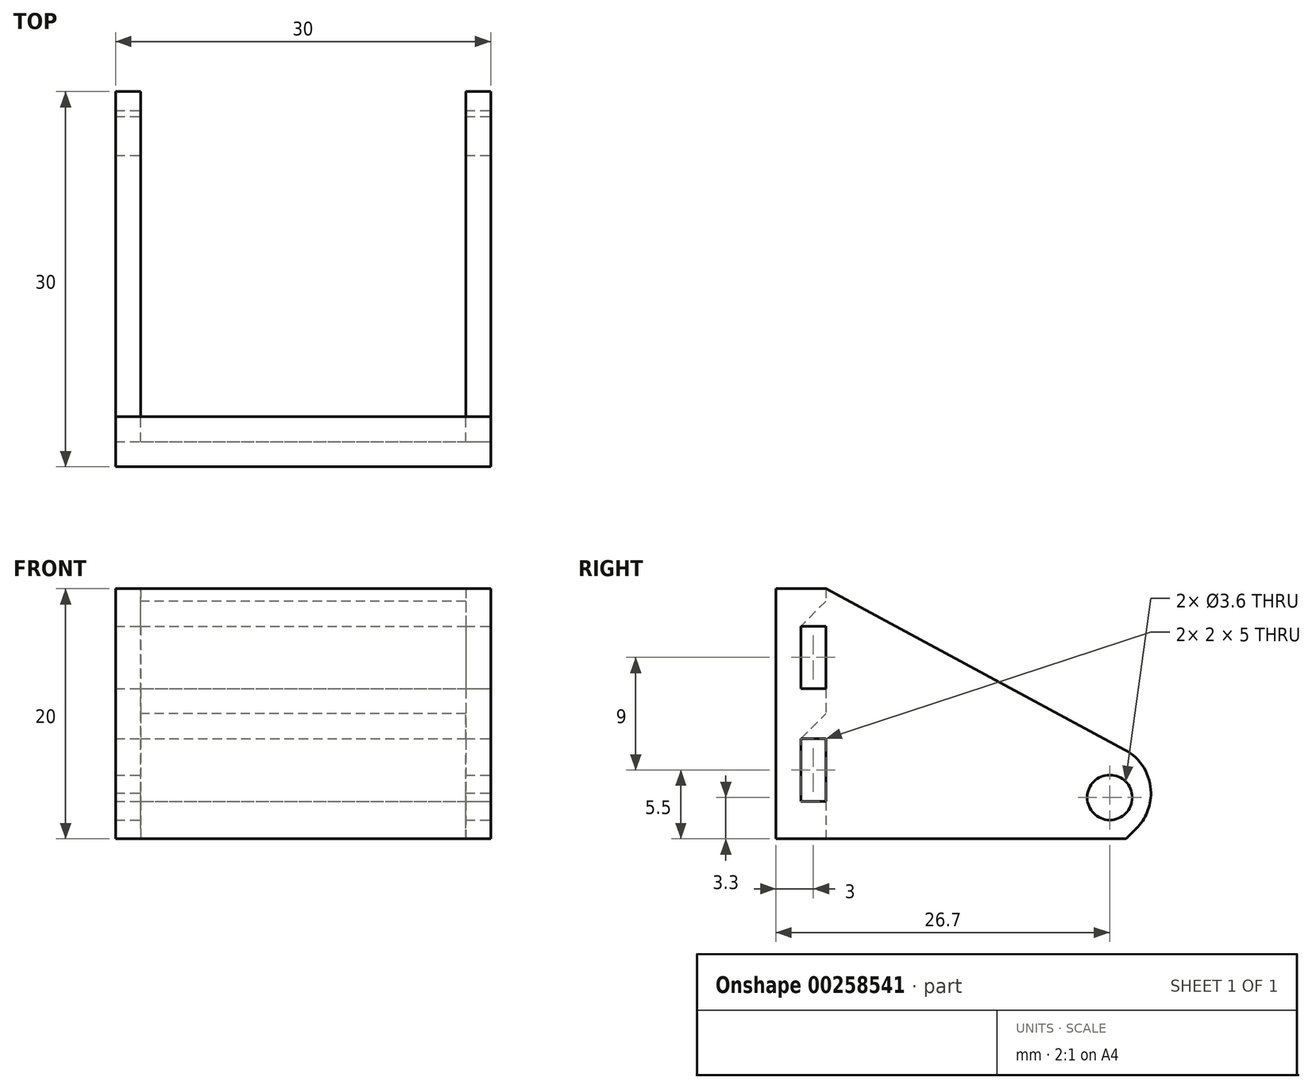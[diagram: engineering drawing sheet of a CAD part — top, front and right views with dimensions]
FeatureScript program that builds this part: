
annotation { "Feature Type Name" : "Feature", "Feature Type Description" : "" }
export const myFeature = defineFeature(function(context is Context, id is Id, definition is map)
    precondition{}
    {
        {
            var Q0;
            Q0=qCreatedBy(makeId("Top.planeOp"),FACE);
            var sketch = newSketch(context, id + "F0", { "sketchPlane" : qUnion([Q0])});
            skLineSegment(sketch, "E0.bottom", {"start": v(13, 13) * mm, "end": v(-13, 13) * mm});
            skLineSegment(sketch, "E0.top", {"start": v(13, -13) * mm, "end": v(-13, -13) * mm});
            skLineSegment(sketch, "E0.left", {"start": v(13, 13) * mm, "end": v(13, -13) * mm});
            skLineSegment(sketch, "E0.right", {"start": v(-13, 13) * mm, "end": v(-13, -13) * mm});
            skPoint(sketch, "E0.middle", {"position": v(0, 0) * mm});
            skLineSegment(sketch, "E1", {"start": v(-13, 13) * mm, "end": v(-15, 13) * mm});
            skLineSegment(sketch, "E2", {"start": v(-15, 13) * mm, "end": v(-15, -17) * mm});
            skLineSegment(sketch, "E3", {"start": v(-15, -17) * mm, "end": v(15, -17) * mm});
            skLineSegment(sketch, "E4", {"start": v(15, -17) * mm, "end": v(15, 13) * mm});
            skLineSegment(sketch, "E5", {"start": v(15, 13) * mm, "end": v(13, 13) * mm});
            skSolve(sketch);
        }
        {
            var Q0;
            Q0=makeQuery(id+"F0.imprint","IMPRINT",FACE,{"disambiguationData":[TD([[makeQuery(id+"F0.imprint","IMPRINT",EDGE,{"derivedFrom":sQuery(id+"F0.wireOp",EDGE,"E0.top")}),1.0]])]});
            extrude(context, id + "F1", {"entities" : qUnion([Q0]), "depth" : 20 * mm});
        }
        {
            var Q0;
            Q0=makeQuery(id+"F1.opExtrude","SWEPT_FACE",FACE,{"disambiguationData":[OSD([sQuery(id+"F0.wireOp",EDGE,"E4")])]});
            var sketch = newSketch(context, id + "F2", { "sketchPlane" : qUnion([Q0])});
            skCircle(sketch, "E6", {"center": v(9.7, 3.3) * mm, "radius": 1.8 * mm});
            skSolve(sketch);
        }
        {
            var Q0;
            Q0=makeQuery(id+"F2.imprint","IMPRINT",FACE,{"disambiguationData":[TD([[makeQuery(id+"F2.imprint","IMPRINT",EDGE,{"derivedFrom":sQuery(id+"F2.wireOp",EDGE,"E6")}),1.0]])]});
            extrude(context, id + "F3", {"entities" : qUnion([Q0]), "operationType" : NewBodyOperationType.REMOVE, "endBound" : BoundingType.THROUGH_ALL, "oppositeDirection" : true, "depth" : 25 * mm});
        }
        {
            var Q0;
            Q0=makeQuery(id+"F1.opExtrude","CAP_EDGE",EDGE,{"disambiguationData":[OSD([sQuery(id+"F0.wireOp",EDGE,"E5")])],"isStart":false});
            var Q1;
            Q1=makeQuery(id+"F1.opExtrude","CAP_EDGE",EDGE,{"disambiguationData":[OSD([sQuery(id+"F0.wireOp",EDGE,"E1")])],"isStart":false});
            chamfer(context, id + "F4", {"entities" : qUnion([Q0, Q1]), "chamferType" : ChamferType.TWO_OFFSETS, "width1" : 26 * mm, "oppositeDirection" : false, "width2" : 14 * mm, "tangentPropagation" : true});
        }
        {
            var Q0;
            Q0=makeQuery(id+"F1.opExtrude","CAP_EDGE",EDGE,{"disambiguationData":[OSD([sQuery(id+"F0.wireOp",EDGE,"E5")])],"isStart":true});
            var Q1;
            Q1=makeQuery(id+"F1.opExtrude","CAP_EDGE",EDGE,{"disambiguationData":[OSD([sQuery(id+"F0.wireOp",EDGE,"E1")])],"isStart":true});
            chamfer(context, id + "F5", {"entities" : qUnion([Q0, Q1]), "width" : 2 * mm, "tangentPropagation" : true});
        }
        {
            var Q0;
            {var subQ0=sQuery(id+"F0.wireOp",EDGE,"E5");Q0=makeQuery(id+"F5.opChamfer","BLEND_EDGE",EDGE,{"blendedFrom":[makeQuery(id+"F1.opExtrude","CAP_EDGE",EDGE,{"disambiguationData":[OSD([subQ0])],"isStart":true}),makeQuery(id+"F1.opExtrude","SWEPT_FACE",FACE,{"disambiguationData":[OSD([subQ0])]})],"blendedInto":[makeQuery(id+"F1.opExtrude","SWEPT_FACE",FACE,{"disambiguationData":[OSD([subQ0])]})]});}
            var Q1;
            {var subQ0=sQuery(id+"F0.wireOp",EDGE,"E1");Q1=makeQuery(id+"F5.opChamfer","BLEND_EDGE",EDGE,{"blendedFrom":[makeQuery(id+"F1.opExtrude","CAP_EDGE",EDGE,{"disambiguationData":[OSD([subQ0])],"isStart":true}),makeQuery(id+"F1.opExtrude","SWEPT_FACE",FACE,{"disambiguationData":[OSD([subQ0])]})],"blendedInto":[makeQuery(id+"F1.opExtrude","SWEPT_FACE",FACE,{"disambiguationData":[OSD([subQ0])]})]});}
            fillet(context, id + "F6", {"entities" : qUnion([Q0, Q1]), "radius" : 4 * mm, "tangentPropagation" : true, "allowEdgeOverflow" : false});
        }
        {
            var Q0;
            {var subQ0=sQuery(id+"F0.wireOp",EDGE,"E5");Q0=makeQuery(id+"F4.opChamfer","BLEND_EDGE",EDGE,{"blendedFrom":[makeQuery(id+"F1.opExtrude","CAP_EDGE",EDGE,{"disambiguationData":[OSD([subQ0])],"isStart":false}),makeQuery(id+"F1.opExtrude","SWEPT_FACE",FACE,{"disambiguationData":[OSD([subQ0])]})],"blendedInto":[makeQuery(id+"F1.opExtrude","SWEPT_FACE",FACE,{"disambiguationData":[OSD([subQ0])]})]});}
            var Q1;
            {var subQ0=sQuery(id+"F0.wireOp",EDGE,"E1");Q1=makeQuery(id+"F4.opChamfer","BLEND_EDGE",EDGE,{"blendedFrom":[makeQuery(id+"F1.opExtrude","CAP_EDGE",EDGE,{"disambiguationData":[OSD([subQ0])],"isStart":false}),makeQuery(id+"F1.opExtrude","SWEPT_FACE",FACE,{"disambiguationData":[OSD([subQ0])]})],"blendedInto":[makeQuery(id+"F1.opExtrude","SWEPT_FACE",FACE,{"disambiguationData":[OSD([subQ0])]})]});}
            fillet(context, id + "F7", {"entities" : qUnion([Q0, Q1]), "radius" : 4 * mm, "tangentPropagation" : true, "allowEdgeOverflow" : false});
        }
        {
            var Q0;
            Q0=makeQuery(id+"F1.opExtrude","SWEPT_FACE",FACE,{"disambiguationData":[OSD([sQuery(id+"F0.wireOp",EDGE,"E4")])]});
            var sketch = newSketch(context, id + "F8", { "sketchPlane" : qUnion([Q0])});
            skLineSegment(sketch, "E7.bottom", {"start": v(-13, 17) * mm, "end": v(-15, 17) * mm});
            skLineSegment(sketch, "E7.top", {"start": v(-13, 12) * mm, "end": v(-15, 12) * mm});
            skLineSegment(sketch, "E7.left", {"start": v(-13, 17) * mm, "end": v(-13, 12) * mm});
            skLineSegment(sketch, "E7.right", {"start": v(-15, 17) * mm, "end": v(-15, 12) * mm});
            skLineSegment(sketch, "E8.bottom", {"start": v(-15, 8) * mm, "end": v(-13, 8) * mm});
            skLineSegment(sketch, "E8.top", {"start": v(-15, 3) * mm, "end": v(-13, 3) * mm});
            skLineSegment(sketch, "E8.left", {"start": v(-15, 8) * mm, "end": v(-15, 3) * mm});
            skLineSegment(sketch, "E8.right", {"start": v(-13, 8) * mm, "end": v(-13, 3) * mm});
            skSolve(sketch);
        }
        {
            var Q0;
            Q0=makeQuery(id+"F8.imprint","IMPRINT",FACE,{"disambiguationData":[TD([[makeQuery(id+"F8.imprint","IMPRINT",EDGE,{"derivedFrom":sQuery(id+"F8.wireOp",EDGE,"E7.bottom")}),1.0]])]});
            var Q1;
            Q1=makeQuery(id+"F8.imprint","IMPRINT",FACE,{"disambiguationData":[TD([[makeQuery(id+"F8.imprint","IMPRINT",EDGE,{"derivedFrom":sQuery(id+"F8.wireOp",EDGE,"E8.bottom")}),-1.0]])]});
            extrude(context, id + "F9", {"entities" : qUnion([Q0, Q1]), "operationType" : NewBodyOperationType.REMOVE, "endBound" : BoundingType.THROUGH_ALL, "oppositeDirection" : true, "depth" : 25 * mm});
        }
        {
            var Q0;
            {var subQ0=sQuery(id+"F8.wireOp",EDGE,"E8.bottom");Q0=makeQuery(id+"F9.boolean.opBoolean","COPY",EDGE,{"disambiguationData":[topologyDisambiguationEdgeConnected([makeQuery(id+"F1.opExtrude","SWEPT_FACE",FACE,{"disambiguationData":[OSD([sQuery(id+"F0.wireOp",EDGE,"E0.top")])]}),makeQuery(id+"F9.opExtrude","SWEPT_FACE",FACE,{"disambiguationData":[OSD([subQ0])]})])],"derivedFrom":makeQuery(id+"F9.opExtrude","SWEPT_EDGE",EDGE,{"disambiguationData":[OSD([subQ0,sQuery(id+"F8.wireOp",EDGE,"E8.right")])]})});}
            var Q1;
            {var subQ0=sQuery(id+"F8.wireOp",EDGE,"E7.bottom");Q1=makeQuery(id+"F9.boolean.opBoolean","COPY",EDGE,{"disambiguationData":[topologyDisambiguationEdgeConnected([makeQuery(id+"F1.opExtrude","SWEPT_FACE",FACE,{"disambiguationData":[OSD([sQuery(id+"F0.wireOp",EDGE,"E0.top")])]}),makeQuery(id+"F9.opExtrude","SWEPT_FACE",FACE,{"disambiguationData":[OSD([subQ0])]})])],"derivedFrom":makeQuery(id+"F9.opExtrude","SWEPT_EDGE",EDGE,{"disambiguationData":[OSD([subQ0,sQuery(id+"F8.wireOp",EDGE,"E7.left")])]})});}
            chamfer(context, id + "F10", {"entities" : qUnion([Q0, Q1]), "width" : 2 * mm, "tangentPropagation" : true});
        }
    });
